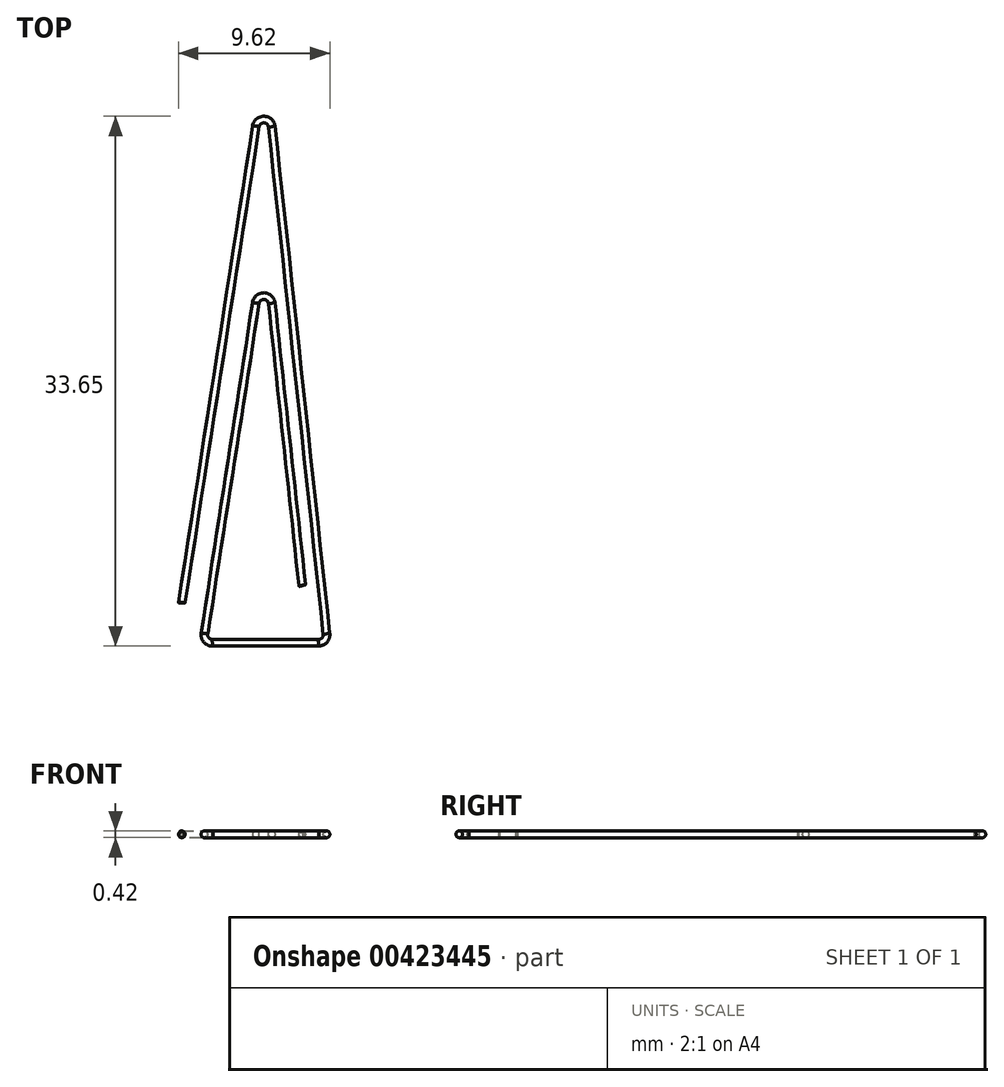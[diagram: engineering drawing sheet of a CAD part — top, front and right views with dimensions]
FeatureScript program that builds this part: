
annotation { "Feature Type Name" : "Feature", "Feature Type Description" : "" }
export const myFeature = defineFeature(function(context is Context, id is Id, definition is map)
    precondition{}
    {
        {
            var Q0;
            Q0=qCreatedBy(makeId("Top.planeOp"),FACE);
            var sketch = newSketch(context, id + "F0", { "sketchPlane" : qUnion([Q0])});
            skLineSegment(sketch, "E0", {"start": v(0, 0) * mm, "end": v(4.7, 30.26) * mm});
            skLineSegment(sketch, "E1", {"start": v(5.71, 30.24) * mm, "end": v(9.2, -1.98) * mm});
            skLineSegment(sketch, "E2", {"start": v(8.69, -2.54) * mm, "end": v(1.94, -2.54) * mm});
            skLineSegment(sketch, "E3", {"start": v(1.44, -1.95) * mm, "end": v(4.7, 19.05) * mm});
            skLineSegment(sketch, "E4", {"start": v(5.71, 19.02) * mm, "end": v(7.65, 1.09) * mm});
            skPoint(sketch, "E5", {"position": v(5.3, -2.54) * mm});
            skPoint(sketch, "E6.visualSharp", {"position": v(1.35, -2.54) * mm});
            skArc(sketch, "E6.filletArc", {"start": v(1.44, -1.95) * mm, "mid": v(1.56, -2.36) * mm, "end": v(1.94, -2.54) * mm});
            skPoint(sketch, "E7.visualSharp", {"position": v(9.25, -2.54) * mm});
            skArc(sketch, "E7.filletArc", {"start": v(8.69, -2.54) * mm, "mid": v(9.06, -2.37) * mm, "end": v(9.2, -1.98) * mm});
            skPoint(sketch, "E8.visualSharp", {"position": v(5.3, 22.86) * mm});
            skArc(sketch, "E8.filletArc", {"start": v(5.71, 19.02) * mm, "mid": v(5.22, 19.48) * mm, "end": v(4.7, 19.05) * mm});
            skPoint(sketch, "E9.visualSharp", {"position": v(5.3, 34.08) * mm});
            skArc(sketch, "E9.filletArc", {"start": v(5.71, 30.24) * mm, "mid": v(5.22, 30.7) * mm, "end": v(4.7, 30.26) * mm});
            skSolve(sketch);
        }
        {
            var Q0;
            Q0=qCreatedBy(makeId("Front.planeOp"),FACE);
            var sketch = newSketch(context, id + "F1", { "sketchPlane" : qUnion([Q0])});
            skCircle(sketch, "E10", {"center": v(0, 0) * mm, "radius": 0.21 * mm});
            skSolve(sketch);
        }
        {
            var Q0;
            Q0 = qSketchRegion(id + "F1", true);
            var Q1;
            Q1 = qConstructionFilter(qBodyType(qCreatedBy(id + "F1" ,EDGE), BodyType.WIRE), ConstructionObject.NO);
            var Q2;
            Q2 = qConstructionFilter(qBodyType(qCreatedBy(id + "F0" ,EDGE), BodyType.WIRE), ConstructionObject.NO);
            sweep(context, id + "F2", {"profiles" : qUnion([Q0]), "surfaceProfiles" : qUnion([Q1]), "path" : qUnion([Q2])});
        }
        {
            var Q0;
            Q0=makeQuery(id+"F2.opSweep","CAP_EDGE",EDGE,{"disambiguationData":[OSD([sQuery(id+"F0.wireOp",VERTEX,"E0.start"),sQuery(id+"F1.wireOp",EDGE,"E10")])],"isStart":true});
            var Q1;
            Q1=makeQuery(id+"F2.opSweep","CAP_FACE",FACE,{"disambiguationData":[OSD([sQuery(id+"F0.wireOp",VERTEX,"E4.end"),sQuery(id+"F1.wireOp",EDGE,"E10")])],"isStart":false});
            fillet(context, id + "F3", {"entities" : qUnion([Q0, Q1]), "radius" : 0.03 * mm, "tangentPropagation" : true, "allowEdgeOverflow" : false});
        }
    });
